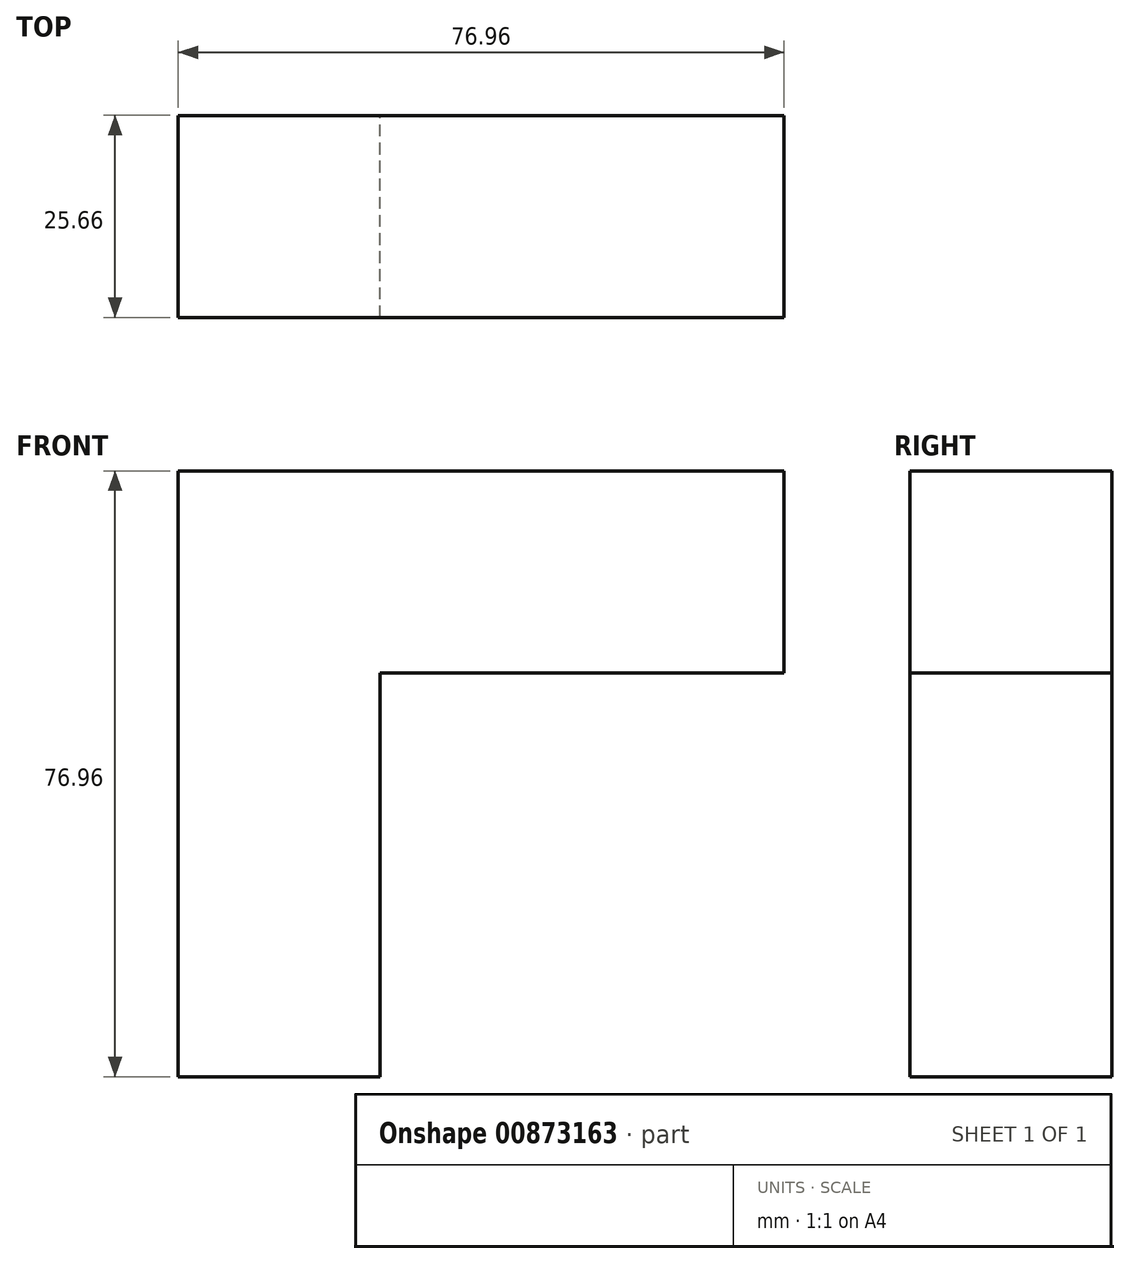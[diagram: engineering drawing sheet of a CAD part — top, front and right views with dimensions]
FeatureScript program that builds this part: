
annotation { "Feature Type Name" : "Feature", "Feature Type Description" : "" }
export const myFeature = defineFeature(function(context is Context, id is Id, definition is map)
    precondition{}
    {
        {
            var Q0;
            Q0=qCreatedBy(makeId("Front.planeOp"),FACE);
            var sketch = newSketch(context, id + "F0", { "sketchPlane" : qUnion([Q0])});
            skLineSegment(sketch, "E0", {"start": v(-54.2, -40.6) * mm, "end": v(-28.55, -40.6) * mm});
            skLineSegment(sketch, "E1", {"start": v(-54.2, -40.6) * mm, "end": v(-54.2, 36.35) * mm});
            skLineSegment(sketch, "E2", {"start": v(-54.2, 36.35) * mm, "end": v(22.75, 36.35) * mm});
            skLineSegment(sketch, "E3", {"start": v(22.75, 36.35) * mm, "end": v(22.75, 10.7) * mm});
            skLineSegment(sketch, "E4", {"start": v(22.75, 10.7) * mm, "end": v(-28.55, 10.7) * mm});
            skLineSegment(sketch, "E5", {"start": v(-28.55, 10.7) * mm, "end": v(-28.55, -40.6) * mm});
            skSolve(sketch);
        }
        {
            var Q0;
            Q0=makeQuery(id+"F0.imprint","IMPRINT",FACE,{"disambiguationData":[TD([[makeQuery(id+"F0.imprint","IMPRINT",EDGE,{"derivedFrom":sQuery(id+"F0.wireOp",EDGE,"E0")}),1.0]])]});
            extrude(context, id + "F1", {"entities" : qUnion([Q0]), "endBound" : BoundingType.SYMMETRIC, "depth" : 25.65 * mm, "offsetDistance" : 25.4 * mm});
        }
    });
